# Revit family: Haworth_Masters_Return_Pedestal
name_source: partatom
category: Furniture Systems
revit_build: Autodesk Revit 2018 (Build: 20170223_1515(x64)
units: mm (PartAtom-declared; Revit-internal decimal feet)

## family parameters
Always vertical = Yes
Cut with Voids When Loaded = No
OmniClass Number = 23.40.70.14.64.21
OmniClass Title = Systems Furniture
Part Type = Normal
Room Calculation Point = No
Round Connector Dimension = Use Diameter
Shared = No
Work Plane-Based = No

## types (1)
- Return
    Actual Depth = 19"
    Actual Height = 29 1/8"
    Actual Width = 42"
    Assembly Code = E2020200
    Bar Pull = No
    Cabinet Finish = Haworth _ Wood _ White Oak
    Classic Pull = Yes
    Custom Size = No
    Depth = 19"
    Description = Haworth - Masters - Return Pedestal
    Drawer Finish = Haworth _ Wood _ White Oak
    Edge Finish = Haworth _ Wood _ White Oak
    Finger Pull = No
    Linear Pull = No
    Manufacturer = Haworth
    Max. Depth = 19"
    Max. Width = 60"
    Min. Depth = 19"
    Min. Width = 42"
    Model = Haworth - Masters - Return Pedestal
    Pedestal Depth = 17"
    Pull Finish = Haworth _ Metal _ Brushed Aluminum
    Revision Number = 2
    Size = Verify Final Dim. w/ Haworth
    Standard Depths = 19 in.
    Standard Widths = 42,48,54,60 in.
    Sustainability Info = http://www.haworth.com
    URL = www.haworth.com
    URL - Product = http://www.haworth.com
    Warranty = http://www.haworth.com
    Width = 42"
    Worksurface Finish = Haworth _ Wood _ White Oak

## geometry (parser evidence)
native form markers: Sweep x12
no freeform markers — native parametric forms only
